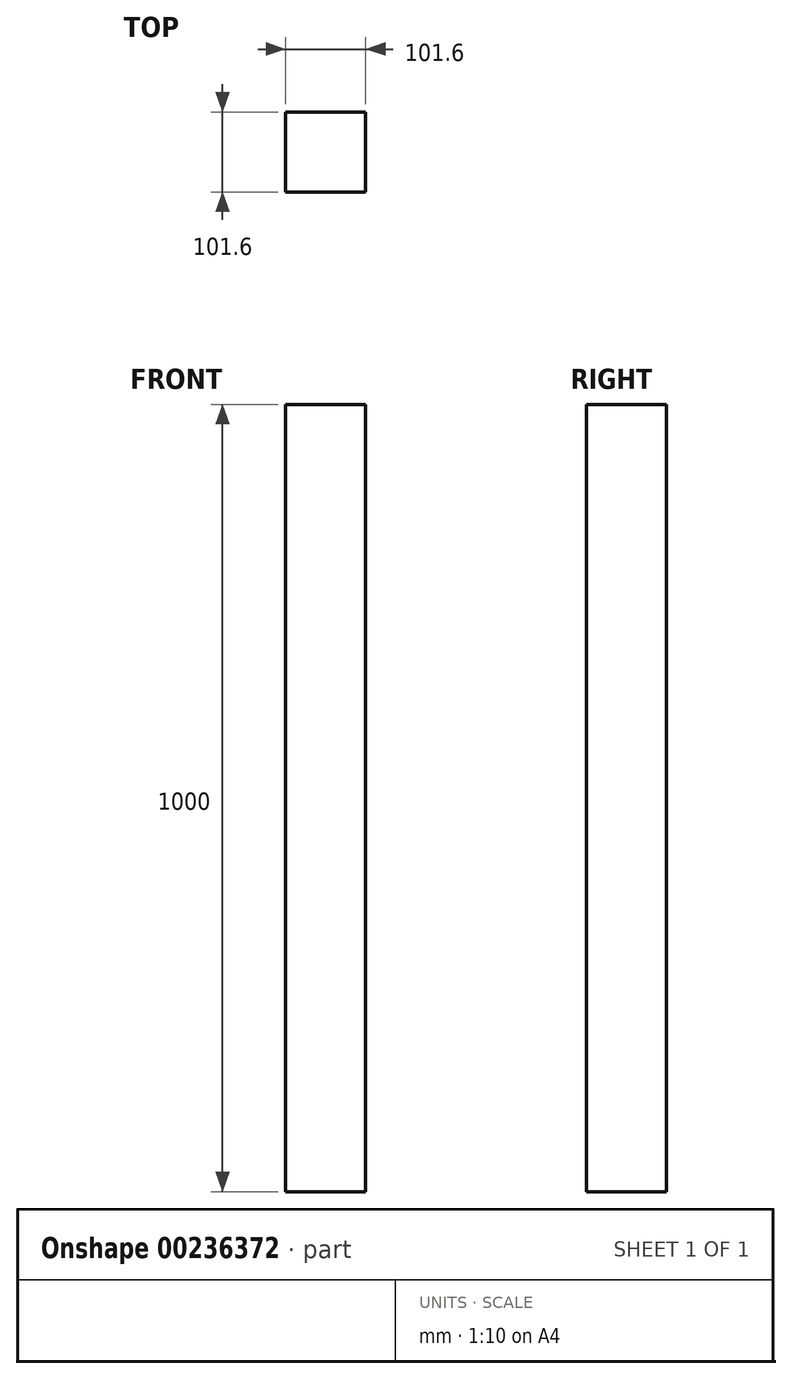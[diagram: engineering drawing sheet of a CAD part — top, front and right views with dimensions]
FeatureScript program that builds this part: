
annotation { "Feature Type Name" : "Feature", "Feature Type Description" : "" }
export const myFeature = defineFeature(function(context is Context, id is Id, definition is map)
    precondition{}
    {
        {
            var Q0;
            Q0=qCreatedBy(makeId("Front.planeOp"),FACE);
            var sketch = newSketch(context, id + "F0", { "sketchPlane" : qUnion([Q0])});
            skLineSegment(sketch, "E0.bottom", {"start": v(-426.47, 510.63) * mm, "end": v(-324.87, 510.63) * mm});
            skLineSegment(sketch, "E0.top", {"start": v(-426.47, -489.37) * mm, "end": v(-324.87, -489.37) * mm});
            skLineSegment(sketch, "E0.left", {"start": v(-426.47, 510.63) * mm, "end": v(-426.47, -489.37) * mm});
            skLineSegment(sketch, "E0.right", {"start": v(-324.87, 510.63) * mm, "end": v(-324.87, -489.37) * mm});
            skSolve(sketch);
        }
        {
            var Q0;
            Q0 = qSketchRegion(id + "F0", true);
            extrude(context, id + "F1", {"entities" : qUnion([Q0]), "depth" : 101.6 * mm});
        }
    });
